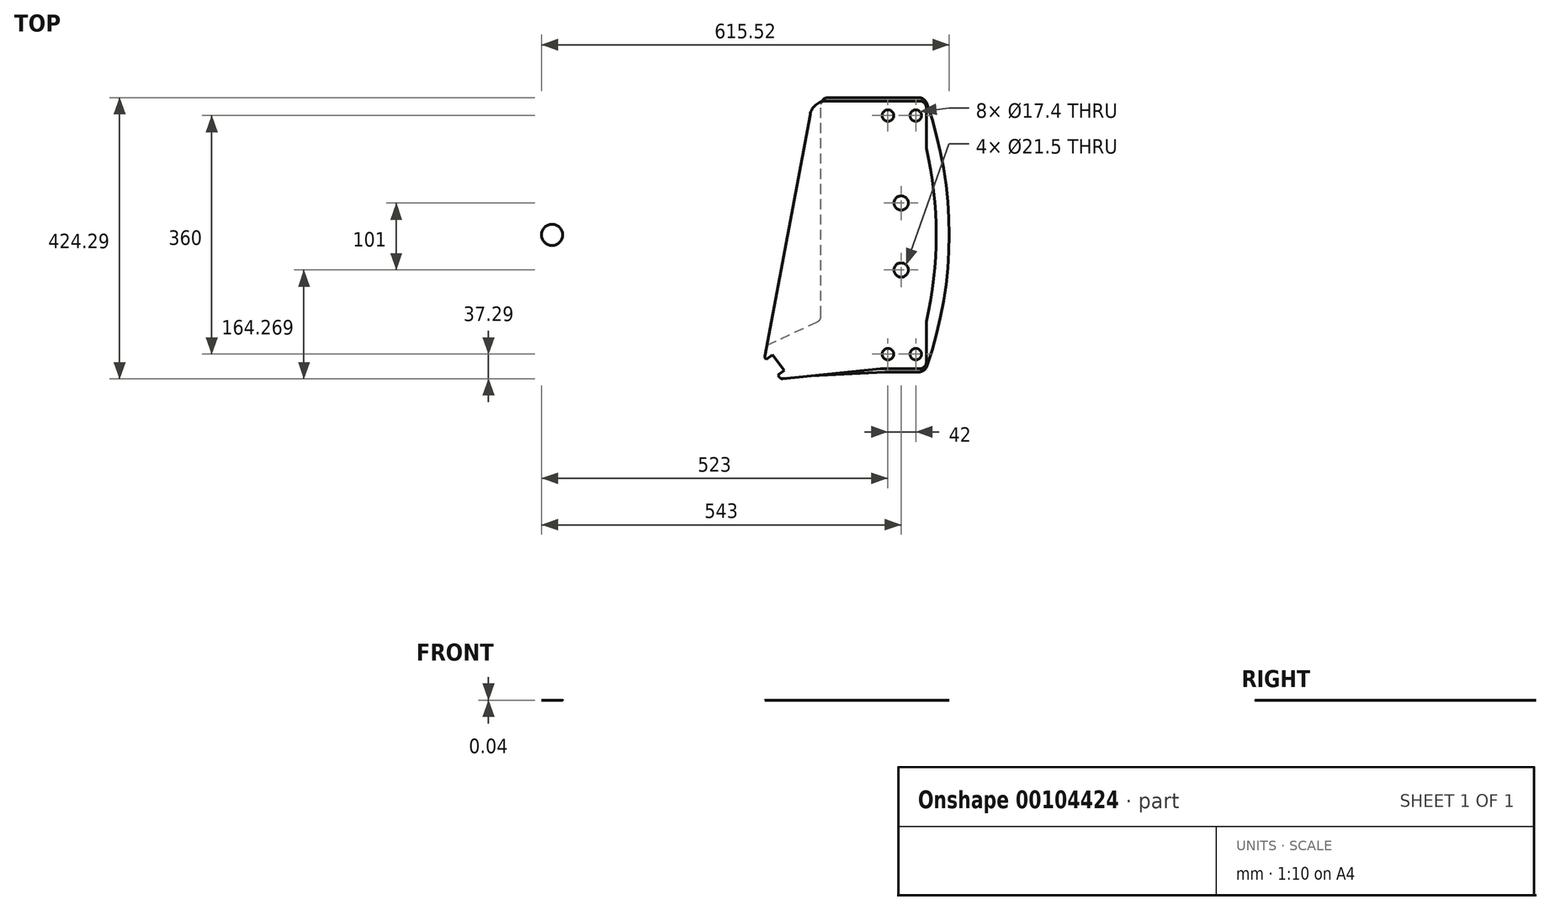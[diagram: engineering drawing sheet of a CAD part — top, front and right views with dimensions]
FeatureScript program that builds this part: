
annotation { "Feature Type Name" : "Feature", "Feature Type Description" : "" }
export const myFeature = defineFeature(function(context is Context, id is Id, definition is map)
    precondition{}
    {
        {
            var Q0;
            Q0=qCreatedBy(makeId("Top.planeOp"),FACE);
            var sketch = newSketch(context, id + "F0", { "sketchPlane" : qUnion([Q0])});
            skCircle(sketch, "E0", {"center": v(507, -180) * mm, "radius": 8.7 * mm});
            skCircle(sketch, "E1", {"center": v(549, -180) * mm, "radius": 8.7 * mm});
            skLineSegment(sketch, "E2", {"start": v(527, 180) * mm, "end": v(527, -180) * mm, "construction": true});
            skLineSegment(sketch, "E3", {"start": v(507, -180) * mm, "end": v(549, -180) * mm, "construction": true});
            skCircle(sketch, "E4", {"center": v(527, 47.98) * mm, "radius": 10.75 * mm});
            skCircle(sketch, "E5", {"center": v(527, -53.02) * mm, "radius": 10.75 * mm});
            skLineSegment(sketch, "E6", {"start": v(0, 0) * mm, "end": v(794.68, -180.83) * mm, "construction": true});
            skLineSegment(sketch, "E7.MirrorCS", {"start": v(0, 0) * mm, "end": v(794.68, 180.83) * mm, "construction": true});
            skLineSegment(sketch, "E8", {"start": v(777.38, -223.05) * mm, "end": v(-17.3, -42.21) * mm, "construction": true});
            skLineSegment(sketch, "E9", {"start": v(827.97, -34.57) * mm, "end": v(794.68, -180.83) * mm, "construction": true});
            skLineSegment(sketch, "E10", {"start": v(827.97, -34.57) * mm, "end": v(798.72, -27.92) * mm, "construction": true});
            skCircle(sketch, "E11", {"center": v(798.72, -27.92) * mm, "radius": 457.2 * mm, "construction": true});
            skLineSegment(sketch, "E12", {"start": v(761.4, 327.1) * mm, "end": v(794.68, 180.83) * mm, "construction": true});
            skLineSegment(sketch, "E13", {"start": v(761.4, 327.1) * mm, "end": v(732.15, 320.44) * mm, "construction": true});
            skCircle(sketch, "E14", {"center": v(732.15, 320.44) * mm, "radius": 615.95 * mm, "construction": true});
            skLineSegment(sketch, "E15", {"start": v(0, 0) * mm, "end": v(527, 0) * mm, "construction": true});
            skCircle(sketch, "E16.MirrorC", {"center": v(507, 180) * mm, "radius": 8.7 * mm});
            skCircle(sketch, "E17.MirrorC", {"center": v(549, 180) * mm, "radius": 8.7 * mm});
            skLineSegment(sketch, "E18", {"start": v(495.7, -202) * mm, "end": v(555, -202) * mm});
            skLineSegment(sketch, "E19", {"start": v(555, 202) * mm, "end": v(414.16, 202) * mm});
            skLineSegment(sketch, "E20", {"start": v(348.22, -217.27) * mm, "end": v(495.7, -202) * mm});
            skLineSegment(sketch, "E21", {"start": v(321.46, -182.98) * mm, "end": v(389.59, 181.6) * mm});
            skArc(sketch, "E22", {"start": v(565, -131.05) * mm, "mid": v(580, 0) * mm, "end": v(565, 131.05) * mm});
            skLineSegment(sketch, "E23", {"start": v(-9.98, 43.88) * mm, "end": v(784.7, 224.71) * mm, "construction": true});
            skPoint(sketch, "E24.visualSharp", {"position": v(393.4, 202) * mm});
            skArc(sketch, "E24.filletArc", {"start": v(414.16, 202) * mm, "mid": v(398.2, 196.23) * mm, "end": v(389.59, 181.6) * mm});
            skPoint(sketch, "E25.visualSharp", {"position": v(543.69, 202) * mm});
            skPoint(sketch, "E26.visualSharp", {"position": v(543.69, -202) * mm});
            skCircle(sketch, "E27", {"center": v(0, 0) * mm, "radius": 16 * mm});
            skLineSegment(sketch, "E28", {"start": v(565, -131.05) * mm, "end": v(565, -192) * mm});
            skPoint(sketch, "E29.visualSharp", {"position": v(565, -202) * mm});
            skArc(sketch, "E29.filletArc", {"start": v(555, -202) * mm, "mid": v(562.07, -199.07) * mm, "end": v(565, -192) * mm});
            skLineSegment(sketch, "E30", {"start": v(565, 131.05) * mm, "end": v(565, 192) * mm});
            skPoint(sketch, "E31.visualSharp", {"position": v(565, 202) * mm});
            skArc(sketch, "E31.filletArc", {"start": v(565, 192) * mm, "mid": v(562.07, 199.07) * mm, "end": v(555, 202) * mm});
            skPoint(sketch, "E32", {"position": v(365.7, -174.65) * mm});
            skLineSegment(sketch, "E33", {"start": v(365.7, -174.65) * mm, "end": v(310.96, -215.77) * mm, "construction": true});
            skLineSegment(sketch, "E34", {"start": v(322.37, -186.9) * mm, "end": v(323.41, -188.28) * mm});
            skLineSegment(sketch, "E35", {"start": v(323.41, -188.28) * mm, "end": v(333, -181.07) * mm});
            skLineSegment(sketch, "E36.MirrorCS", {"start": v(340.83, -211.47) * mm, "end": v(350.42, -204.26) * mm});
            skLineSegment(sketch, "E37", {"start": v(333, -181.07) * mm, "end": v(350.42, -204.26) * mm});
            skLineSegment(sketch, "E38.trimOffspring", {"start": v(340.83, -211.47) * mm, "end": v(343.7, -215.3) * mm});
            skPoint(sketch, "E39.visualSharp", {"position": v(345.4, -217.56) * mm});
            skArc(sketch, "E39.filletArc", {"start": v(343.7, -215.3) * mm, "mid": v(345.7, -216.87) * mm, "end": v(348.22, -217.27) * mm});
            skPoint(sketch, "E40.visualSharp", {"position": v(321.05, -185.14) * mm});
            skArc(sketch, "E40.filletArc", {"start": v(321.46, -182.98) * mm, "mid": v(321.5, -185.03) * mm, "end": v(322.37, -186.9) * mm});
            skSolve(sketch);
        }
        {
            var Q0;
            Q0=makeQuery(id+"F0.imprint","IMPRINT",FACE,{"disambiguationData":[TD([[makeQuery(id+"F0.imprint","IMPRINT",EDGE,{"derivedFrom":sQuery(id+"F0.wireOp",EDGE,"ebD0Zzvh-qBuO-ddLj-7H2e-9OK9i4GohCq1")}),1.0]])]});
            var Q1;
            Q1=makeQuery(id+"F0.imprint","IMPRINT",FACE,{"disambiguationData":[TD([[makeQuery(id+"F0.imprint","IMPRINT",EDGE,{"derivedFrom":sQuery(id+"F0.wireOp",EDGE,"E0")}),-1.0]])]});
            extrude(context, id + "F1", {"entities" : qUnion([Q0, Q1]), "offsetDistance" : 25 * mm, "depth" : 9 / 406.4 * mm});
        }
        {
            var Q0;
            Q0=makeQuery(id+"F1.opExtrude","CAP_FACE",FACE,{"disambiguationData":[OSD([sQuery(id+"F0.wireOp",EDGE,"E0"),sQuery(id+"F0.wireOp",EDGE,"E1"),sQuery(id+"F0.wireOp",EDGE,"E4"),sQuery(id+"F0.wireOp",EDGE,"E5"),sQuery(id+"F0.wireOp",EDGE,"E16.MirrorC"),sQuery(id+"F0.wireOp",EDGE,"E17.MirrorC"),sQuery(id+"F0.wireOp",EDGE,"E18"),sQuery(id+"F0.wireOp",EDGE,"E19"),sQuery(id+"F0.wireOp",EDGE,"v8oQM6Ld-WJjn-TjKk-qOQu-YLSsJ02fWpNw"),sQuery(id+"F0.wireOp",EDGE,"E20"),sQuery(id+"F0.wireOp",EDGE,"E21"),sQuery(id+"F0.wireOp",EDGE,"E22"),sQuery(id+"F0.wireOp",EDGE,"35b93844-582d-4247-a7bc-7ac831969438.filletArc"),sQuery(id+"F0.wireOp",EDGE,"2c13d87a-717a-4858-a9f2-86daaeaa72ff.filletArc"),sQuery(id+"F0.wireOp",EDGE,"E24.filletArc"),sQuery(id+"F0.wireOp",EDGE,"E25.filletArc"),sQuery(id+"F0.wireOp",EDGE,"E26.filletArc")])],"isStart":true});
            var sketch = newSketch(context, id + "F2", { "sketchPlane" : qUnion([Q0])});
            skLineSegment(sketch, "E41.3", {"start": v(553.08, -207) * mm, "end": v(416.03, -207) * mm});
            skArc(sketch, "E41.4", {"start": v(565.91, -197.9) * mm, "mid": v(560.95, -204.5) * mm, "end": v(553.08, -207) * mm});
            skArc(sketch, "E41.5", {"start": v(565.91, 197.9) * mm, "mid": v(599.52, 0) * mm, "end": v(565.91, -197.9) * mm});
            skArc(sketch, "E41.9", {"start": v(553.08, 207) * mm, "mid": v(560.95, 204.5) * mm, "end": v(565.91, 197.9) * mm});
            skCircle(sketch, "E42", {"center": v(507, 180) * mm, "radius": 8.7 * mm});
            skCircle(sketch, "E43", {"center": v(549, 180) * mm, "radius": 8.7 * mm});
            skCircle(sketch, "E44", {"center": v(527, 53.02) * mm, "radius": 10.75 * mm});
            skCircle(sketch, "E45", {"center": v(527, -47.98) * mm, "radius": 10.75 * mm});
            skCircle(sketch, "E46", {"center": v(507, -180) * mm, "radius": 8.7 * mm});
            skCircle(sketch, "E47", {"center": v(549, -180) * mm, "radius": 8.7 * mm});
            skLineSegment(sketch, "E48", {"start": v(502.46, 207) * mm, "end": v(553.08, 207) * mm});
            skPoint(sketch, "E49", {"position": v(430.13, -157.77) * mm});
            skLineSegment(sketch, "E50", {"start": v(324.56, 166.38) * mm, "end": v(400.22, 131.39) * mm});
            skLineSegment(sketch, "E51", {"start": v(406.03, 122.31) * mm, "end": v(406.03, -197) * mm});
            skArc(sketch, "E52.filletArc", {"start": v(406.03, -197) * mm, "mid": v(408.96, -204.07) * mm, "end": v(416.03, -207) * mm});
            skPoint(sketch, "E53.visualSharp", {"position": v(406.03, 112.52) * mm});
            skArc(sketch, "E53.filletArc", {"start": v(406.03, 122.31) * mm, "mid": v(404.45, 127.7) * mm, "end": v(400.22, 131.39) * mm});
            skLineSegment(sketch, "E54", {"start": v(324.56, 166.38) * mm, "end": v(321.46, 182.98) * mm});
            skLineSegment(sketch, "E55", {"start": v(321.46, 182.98) * mm, "end": v(323.41, 188.28) * mm});
            skLineSegment(sketch, "E56", {"start": v(323.41, 188.28) * mm, "end": v(333, 181.07) * mm});
            skLineSegment(sketch, "E57", {"start": v(333, 181.07) * mm, "end": v(350.42, 204.26) * mm});
            skLineSegment(sketch, "E58", {"start": v(350.42, 204.26) * mm, "end": v(340.83, 211.47) * mm});
            skLineSegment(sketch, "E59", {"start": v(340.83, 211.47) * mm, "end": v(343.7, 215.3) * mm});
            skLineSegment(sketch, "E60", {"start": v(343.7, 215.3) * mm, "end": v(502.46, 207) * mm});
            skSolve(sketch);
        }
        {
            var Q0;
            Q0 = qSketchRegion(id + "F2", true);
            extrude(context, id + "F3", {"entities" : qUnion([Q0]), "depth" : 9 / 406.4 * mm});
        }
        {
            var Q0;
            Q0=makeQuery(id+"F0.imprint","IMPRINT",FACE,{"disambiguationData":[TD([[makeQuery(id+"F0.imprint","IMPRINT",EDGE,{"derivedFrom":sQuery(id+"F0.wireOp",EDGE,"E27")}),1.0]])]});
            extrude(context, id + "F4", {"entities" : qUnion([Q0]), "depth" : 9 / 406.4 * mm, "offsetDistance" : 25 * mm});
        }
    });
